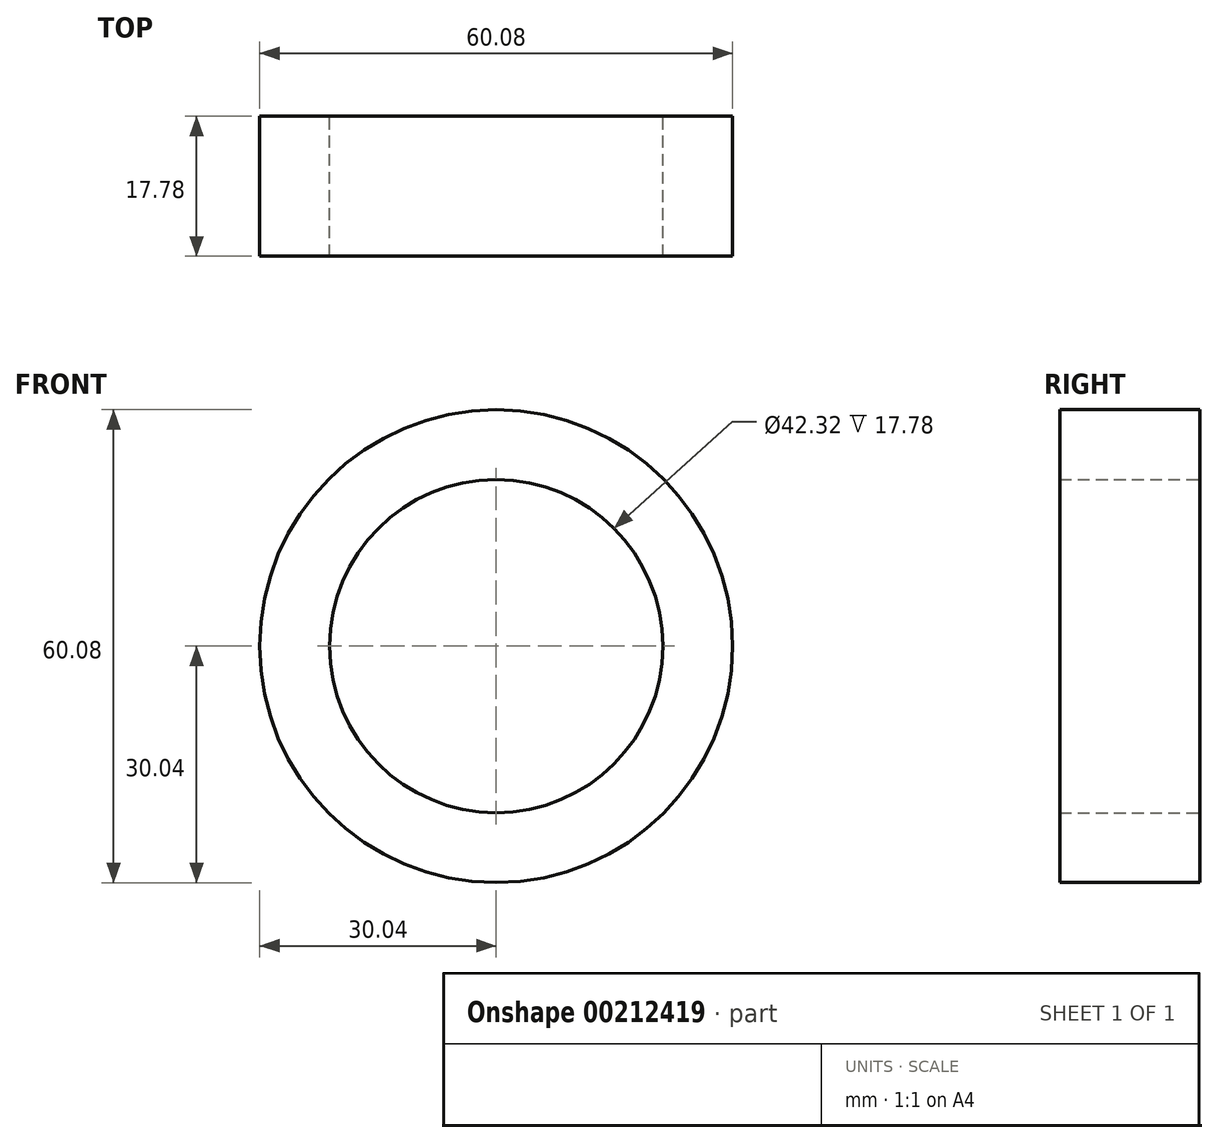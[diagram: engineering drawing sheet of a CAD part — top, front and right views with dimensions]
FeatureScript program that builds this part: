
annotation { "Feature Type Name" : "Feature", "Feature Type Description" : "" }
export const myFeature = defineFeature(function(context is Context, id is Id, definition is map)
    precondition{}
    {
        {
            var Q0;
            Q0=qCreatedBy(makeId("Front.planeOp"),FACE);
            var sketch = newSketch(context, id + "F0", { "sketchPlane" : qUnion([Q0])});
            skCircle(sketch, "E0", {"center": v(0, 0) * mm, "radius": 30.04 * mm});
            skCircle(sketch, "E1", {"center": v(0, 0) * mm, "radius": 21.16 * mm});
            skSolve(sketch);
        }
        {
            var Q0;
            Q0 = qSketchRegion(id + "F0", true);
            extrude(context, id + "F1", {"entities" : qUnion([Q0]), "depth" : 17.78 * mm});
        }
    });
